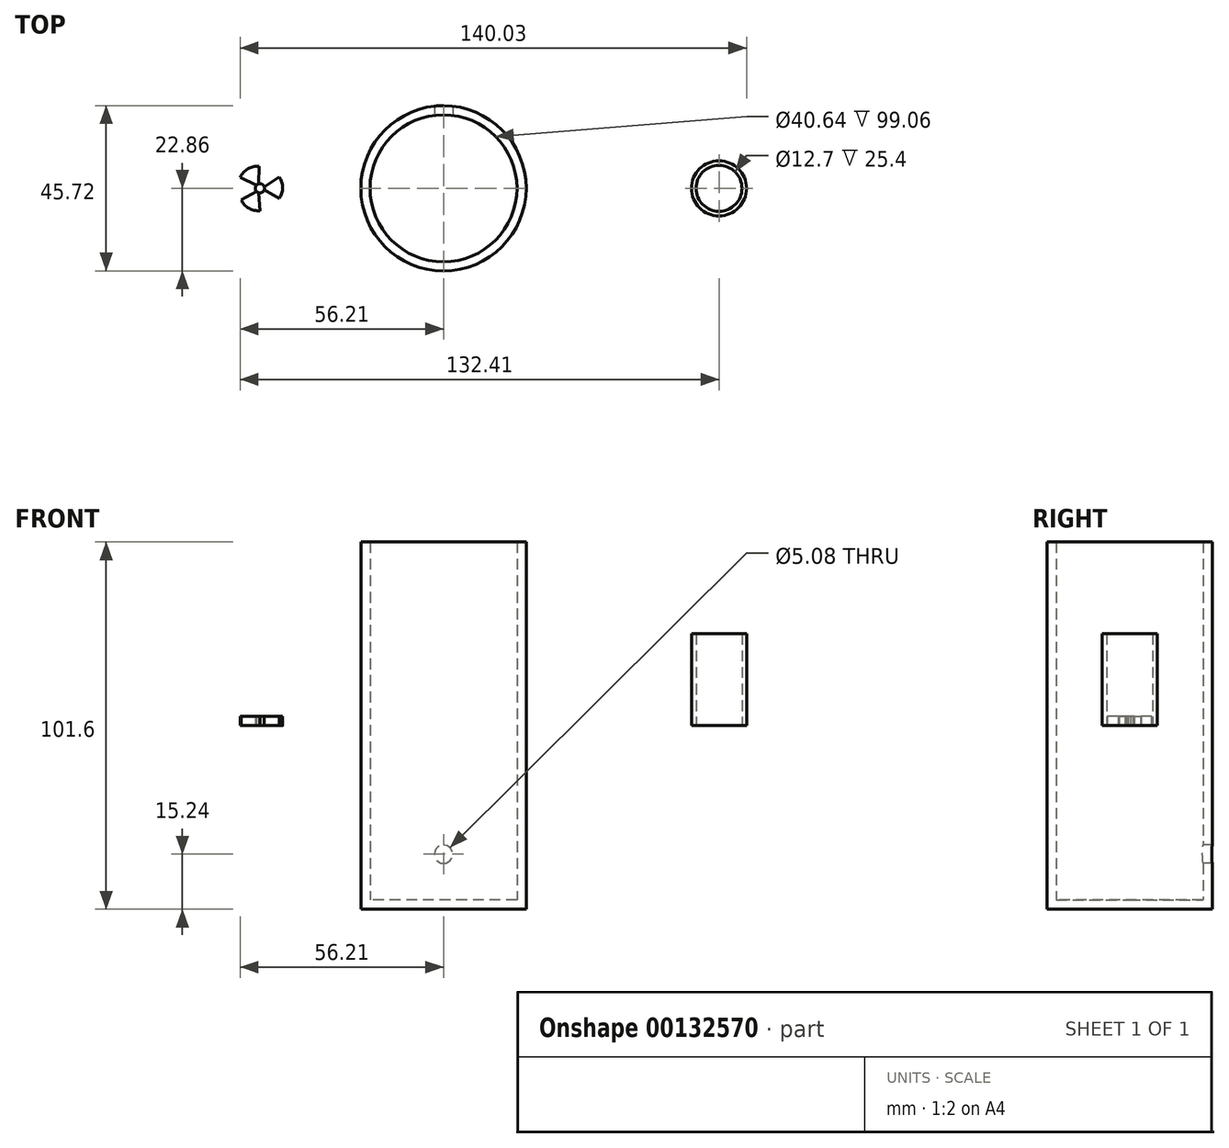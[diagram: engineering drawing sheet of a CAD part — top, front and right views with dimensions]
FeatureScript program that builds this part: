
annotation { "Feature Type Name" : "Feature", "Feature Type Description" : "" }
export const myFeature = defineFeature(function(context is Context, id is Id, definition is map)
    precondition{}
    {
        {
            var Q0;
            Q0=qCreatedBy(makeId("Top.planeOp"),FACE);
            var sketch = newSketch(context, id + "F0", { "sketchPlane" : qUnion([Q0])});
            skCircle(sketch, "E0", {"center": v(0, 0) * mm, "radius": 22.86 * mm});
            skSolve(sketch);
        }
        {
            var Q0;
            Q0=makeQuery(id+"F0.imprint","IMPRINT",FACE,{"disambiguationData":[TD([[makeQuery(id+"F0.imprint","IMPRINT",EDGE,{"derivedFrom":sQuery(id+"F0.wireOp",EDGE,"E0")}),1.0]])]});
            extrude(context, id + "F1", {"entities" : qUnion([Q0]), "endBound" : BoundingType.SYMMETRIC, "depth" : 101.6 * mm});
        }
        {
            var Q0;
            Q0=makeQuery(id+"F1.opExtrude","CAP_FACE",FACE,{"disambiguationData":[OSD([sQuery(id+"F0.wireOp",EDGE,"E0")])],"isStart":false});
            var Q1;
            Q1=makeQuery(id+"F1.opExtrude","SWEPT_BODY",BODY,{"disambiguationData":[OSD([sQuery(id+"F0.wireOp",EDGE,"E0")])]});
            shell(context, id + "F2", {"entities" : qUnion([Q0]), "parts" : qUnion([Q1]), "thickness" : 2.54 * mm});
        }
        {
            var Q0;
            Q0=qCreatedBy(makeId("Front.planeOp"),FACE);
            var sketch = newSketch(context, id + "F3", { "sketchPlane" : qUnion([Q0])});
            skCircle(sketch, "E1", {"center": v(0, -35.56) * mm, "radius": 2.54 * mm});
            skSolve(sketch);
        }
        {
            var Q0;
            Q0 = qSketchRegion(id + "F3", true);
            var Q1;
            Q1=sQuery(id+"F3.wireOp",EDGE,"E1");
            extrude(context, id + "F4", {"entities" : qUnion([Q0]), "operationType" : NewBodyOperationType.REMOVE, "surfaceEntities" : qUnion([Q1]), "oppositeDirection" : true, "depth" : 22.95 * mm});
        }
        {
            var Q0;
            Q0=qCreatedBy(makeId("Top.planeOp"),FACE);
            var sketch = newSketch(context, id + "F5", { "sketchPlane" : qUnion([Q0])});
            skCircle(sketch, "E2", {"center": v(76.2, 0) * mm, "radius": 7.62 * mm});
            skSolve(sketch);
        }
        {
            var Q0;
            Q0=makeQuery(id+"F5.imprint","IMPRINT",FACE,{"disambiguationData":[TD([[makeQuery(id+"F5.imprint","IMPRINT",EDGE,{"derivedFrom":sQuery(id+"F5.wireOp",EDGE,"E2")}),1.0]])]});
            var Q1;
            Q1=sQuery(id+"F5.wireOp",EDGE,"E2");
            extrude(context, id + "F6", {"entities" : qUnion([Q0]), "surfaceEntities" : qUnion([Q1]), "depth" : 25.4 * mm});
        }
        {
            var Q0;
            Q0=makeQuery(id+"F6.opExtrude","CAP_FACE",FACE,{"disambiguationData":[OSD([sQuery(id+"F5.wireOp",EDGE,"E2")])],"isStart":true});
            var sketch = newSketch(context, id + "F7", { "sketchPlane" : qUnion([Q0])});
            skCircle(sketch, "E3", {"center": v(76.2, 0) * mm, "radius": 6.35 * mm});
            skSolve(sketch);
        }
        {
            var Q0;
            Q0=makeQuery(id+"F7.imprint","IMPRINT",FACE,{"disambiguationData":[TD([[makeQuery(id+"F7.imprint","IMPRINT",EDGE,{"derivedFrom":sQuery(id+"F7.wireOp",EDGE,"E3")}),1.0]])]});
            extrude(context, id + "F8", {"entities" : qUnion([Q0]), "operationType" : NewBodyOperationType.REMOVE, "oppositeDirection" : true, "depth" : 25.4 * mm});
        }
        {
            var Q0;
            Q0=qCreatedBy(makeId("Top.planeOp"),FACE);
            var sketch = newSketch(context, id + "F9", { "sketchPlane" : qUnion([Q0])});
            skCircle(sketch, "E4", {"center": v(-50.8, 0) * mm, "radius": 1.27 * mm});
            skSolve(sketch);
        }
        {
            var Q0;
            Q0=makeQuery(id+"F9.imprint","IMPRINT",FACE,{"disambiguationData":[TD([[makeQuery(id+"F9.imprint","IMPRINT",EDGE,{"derivedFrom":sQuery(id+"F9.wireOp",EDGE,"E4")}),1.0]])]});
            extrude(context, id + "F10", {"entities" : qUnion([Q0]), "depth" : 2.54 * mm});
        }
        {
            var Q0;
            Q0=qCreatedBy(makeId("Top.planeOp"),FACE);
            var sketch = newSketch(context, id + "F11", { "sketchPlane" : qUnion([Q0])});
            skCircle(sketch, "E5.0", {"center": v(-50.8, 0) * mm, "radius": 1.27 * mm});
            skLineSegment(sketch, "E6", {"start": v(-49.58, 0.34) * mm, "end": v(-45.46, 3.16) * mm});
            skLineSegment(sketch, "E7", {"start": v(-45.46, -2.84) * mm, "end": v(-49.59, -0.38) * mm});
            skLineSegment(sketch, "E8", {"start": v(-49.59, -0.38) * mm, "end": v(-49.58, 0.34) * mm});
            skArc(sketch, "E9", {"start": v(-45.46, -2.84) * mm, "mid": v(-44.5, 0.16) * mm, "end": v(-45.46, 3.16) * mm});
            skSolve(sketch);
        }
        {
            var Q0;
            {var subQ1=sQuery(id+"F11.wireOp",EDGE,"E6");Q0=makeQuery(id+"F11.imprint","IMPRINT",FACE,{"disambiguationData":[TD([[makeQuery(id+"F11.imprint","IMPRINT",EDGE,{"derivedFrom":subQ1}),-1.0]])]});}
            extrude(context, id + "F12", {"entities" : qUnion([Q0]), "operationType" : NewBodyOperationType.ADD, "depth" : 2.54 * mm});
        }
        {
            var Q0;
            Q0=makeQuery(id+"F10.opExtrude","SWEPT_BODY",BODY,{"disambiguationData":[OSD([sQuery(id+"F9.wireOp",EDGE,"E4")])]});
            var Q1;
            Q1=makeQuery(id+"F10.opExtrude","SWEPT_FACE",FACE,{"disambiguationData":[OSD([sQuery(id+"F9.wireOp",EDGE,"E4")])]});
            circularPattern(context, id + "F13", {"operationType" : NewBodyOperationType.ADD, "entities" : qUnion([Q0]), "axis" : qUnion([Q1]), "angle" : 120 * degree, "instanceCount" : 3});
        }
    });
